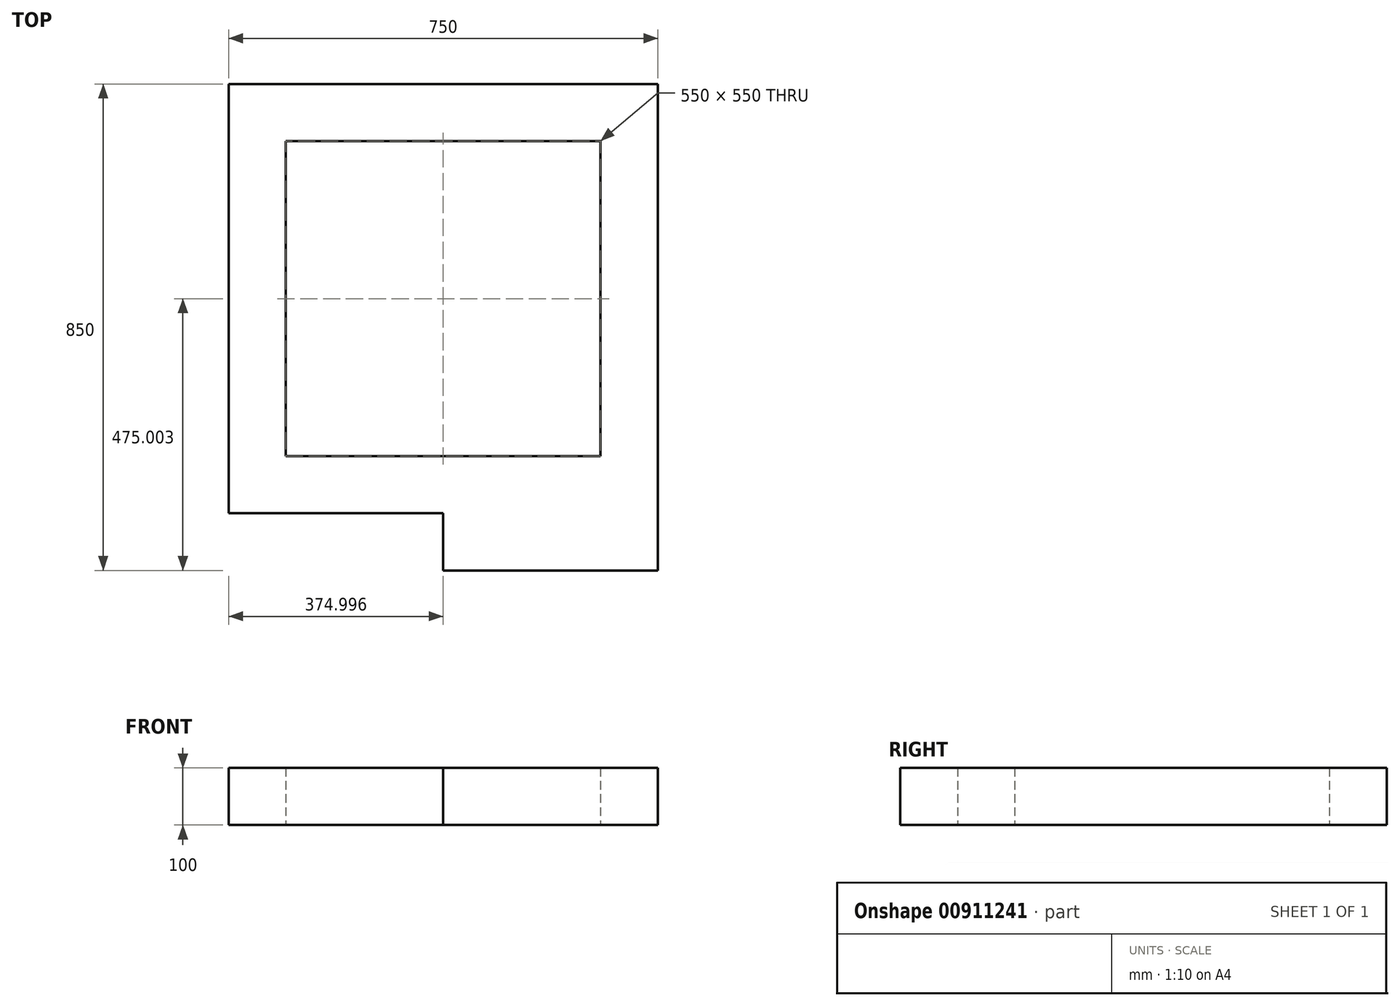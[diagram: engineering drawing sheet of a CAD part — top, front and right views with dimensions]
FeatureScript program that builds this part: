
annotation { "Feature Type Name" : "Feature", "Feature Type Description" : "" }
export const myFeature = defineFeature(function(context is Context, id is Id, definition is map)
    precondition{}
    {
        {
            var Q0;
            Q0=qCreatedBy(makeId("Top.planeOp"),FACE);
            var sketch = newSketch(context, id + "F0", { "sketchPlane" : qUnion([Q0])});
            skLineSegment(sketch, "E0.bottom", {"start": v(-130.62, -47) * mm, "end": v(619.38, -47) * mm});
            skLineSegment(sketch, "E0.top", {"start": v(-130.62, 703) * mm, "end": v(619.38, 703) * mm});
            skLineSegment(sketch, "E0.left", {"start": v(-130.62, -47) * mm, "end": v(-130.62, 703) * mm});
            skLineSegment(sketch, "E0.right", {"start": v(619.38, -47) * mm, "end": v(619.38, 703) * mm});
            skLineSegment(sketch, "E1.0", {"start": v(-30.62, 53) * mm, "end": v(519.38, 53) * mm});
            skLineSegment(sketch, "E2.0", {"start": v(-30.62, 53) * mm, "end": v(-30.62, 603) * mm});
            skLineSegment(sketch, "E3.0", {"start": v(-30.62, 603) * mm, "end": v(519.38, 603) * mm});
            skLineSegment(sketch, "E4.0", {"start": v(519.38, 53) * mm, "end": v(519.38, 603) * mm});
            skSolve(sketch);
        }
        {
            var Q0;
            Q0 = qSketchRegion(id + "F0", true);
            extrude(context, id + "F1", {"entities" : qUnion([Q0]), "depth" : 100 * mm, "offsetDistance" : 25 * mm});
        }
        {
            var Q0;
            Q0=makeQuery(id+"F1.opExtrude","SWEPT_FACE",FACE,{"disambiguationData":[OSD([sQuery(id+"F0.wireOp",EDGE,"E0.bottom")])]});
            var sketch = newSketch(context, id + "F2", { "sketchPlane" : qUnion([Q0])});
            skLineSegment(sketch, "E5", {"start": v(-130.62, 50) * mm, "end": v(619.38, 50) * mm});
            skLineSegment(sketch, "E6", {"start": v(244.38, 100) * mm, "end": v(244.38, 0) * mm});
            skCircle(sketch, "E7", {"center": v(244.38, 50) * mm, "radius": 10 * mm});
            skSolve(sketch);
        }
        {
            var Q0;
            {var subQ0=sQuery(id+"F2.wireOp",EDGE,"E6");var subQ1=sQuery(id+"F2.wireOp",EDGE,"E5");var subQ2=makeQuery(id+"F2.imprint","INTERSECT",VERTEX,{"derivedFrom":[subQ1,subQ0]});Q0=makeQuery(id+"F2.imprint","IMPRINT",FACE,{"disambiguationData":[TD([[makeQuery(id+"F2.imprint","IMPRINT",EDGE,{"disambiguationData":[TD([[subQ2,-1.0]])],"derivedFrom":subQ1}),1.0]])]});}
            var Q1;
            {var subQ0=sQuery(id+"F2.wireOp",EDGE,"E7");var subQ1=sQuery(id+"F2.wireOp",EDGE,"E5");var subQ2=makeQuery(id+"F2.imprint","INTERSECT",VERTEX,{"disambiguationData":[OD(0.0)],"derivedFrom":[subQ1,subQ0]});Q1=makeQuery(id+"F2.imprint","IMPRINT",FACE,{"disambiguationData":[TD([[makeQuery(id+"F2.imprint","IMPRINT",EDGE,{"disambiguationData":[TD([[subQ2,-1.0]])],"derivedFrom":subQ1}),1.0]])]});}
            var Q2;
            {var subQ0=sQuery(id+"F2.wireOp",EDGE,"E7");var subQ1=sQuery(id+"F2.wireOp",EDGE,"E5");var subQ2=makeQuery(id+"F2.imprint","INTERSECT",VERTEX,{"disambiguationData":[OD(0.0)],"derivedFrom":[subQ1,subQ0]});Q2=makeQuery(id+"F2.imprint","IMPRINT",FACE,{"disambiguationData":[TD([[makeQuery(id+"F2.imprint","IMPRINT",EDGE,{"disambiguationData":[TD([[subQ2,-1.0]])],"derivedFrom":subQ1}),-1.0]])]});}
            var Q3;
            {var subQ0=sQuery(id+"F2.wireOp",EDGE,"E6");var subQ1=sQuery(id+"F2.wireOp",EDGE,"E5");var subQ2=makeQuery(id+"F2.imprint","INTERSECT",VERTEX,{"derivedFrom":[subQ1,subQ0]});Q3=makeQuery(id+"F2.imprint","IMPRINT",FACE,{"disambiguationData":[TD([[makeQuery(id+"F2.imprint","IMPRINT",EDGE,{"disambiguationData":[TD([[subQ2,-1.0]])],"derivedFrom":subQ1}),-1.0]])]});}
            extrude(context, id + "F3", {"entities" : qUnion([Q0, Q1, Q2, Q3]), "operationType" : NewBodyOperationType.ADD, "depth" : 100 * mm, "offsetDistance" : 25 * mm});
        }
    });
